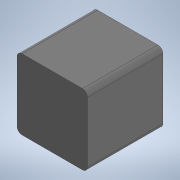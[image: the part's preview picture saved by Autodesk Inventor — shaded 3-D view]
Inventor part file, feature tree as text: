
AUTODESK INVENTOR PART (.ipt)
format: ipt  version: 2022 (Build 260153000, 153)  size: 99,840 bytes
history: native  units: in
note: dims shown in document units (in); Inventor stores cm internally (conversion verified against a paired STEP export)
features: extrude x1, fillet x1, sketch x1
ambient origin geometry x8: Origin, YZ Plane, XZ Plane, XY Plane, X Axis, Y Axis, Z Axis, Center Point
bodies: Solid1 (feature_tree)
feature tree (3):
  extrude  "Extrusion1"  Depth=1.1024in
  fillet  "Fillet1"  Radius=1.1811in
  sketch  "Sketch1"  dims[d0=1.1024in d1=1.1024in d2=1.1811in d3=0.0in d4=0.0787in]
